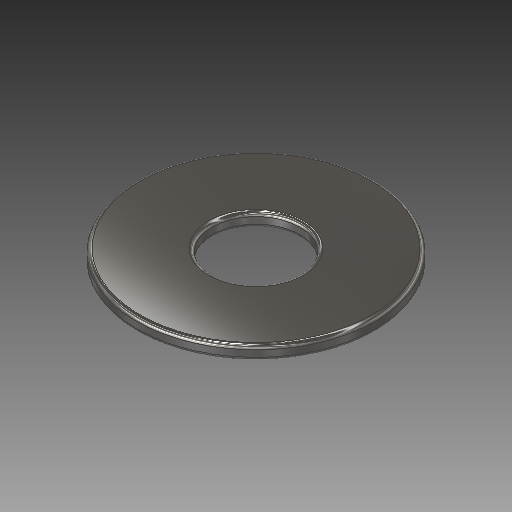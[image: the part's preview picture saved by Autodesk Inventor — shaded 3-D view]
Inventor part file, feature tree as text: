
AUTODESK INVENTOR PART (.ipt)
format: ipt  version: 2019 (Build 230136000, 136)  size: 143,872 bytes
history: native  units: mm
features: other x1, revolve x1, fillet x1, sketch x1
ambient origin geometry x8: Origin, YZ Plane, XZ Plane, XY Plane, X Axis, Y Axis, Z Axis, Center Point
bodies: Body1 (feature_tree)
feature tree (4):
  other  "Твердое тело1"
  revolve  "Вращение1"
  fillet  "Сопряжение3"  Radius=26.0mm
  sketch  "Эскиз1"
